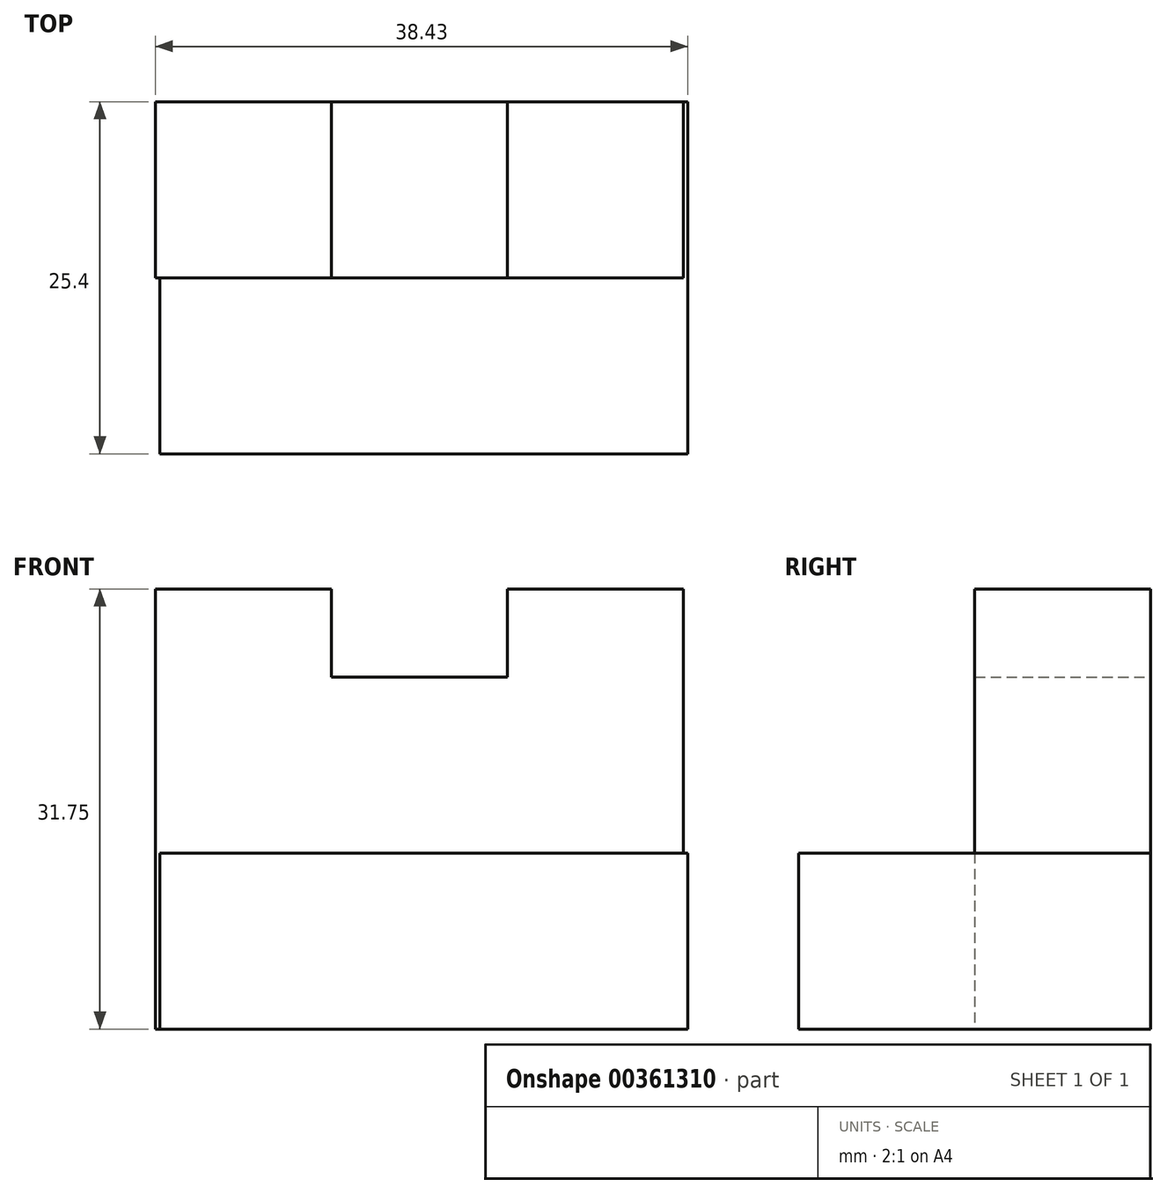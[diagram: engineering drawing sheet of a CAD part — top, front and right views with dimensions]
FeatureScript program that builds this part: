
annotation { "Feature Type Name" : "Feature", "Feature Type Description" : "" }
export const myFeature = defineFeature(function(context is Context, id is Id, definition is map)
    precondition{}
    {
        {
            var Q0;
            Q0=qCreatedBy(makeId("Front.planeOp"),FACE);
            var sketch = newSketch(context, id + "F0", { "sketchPlane" : qUnion([Q0])});
            skLineSegment(sketch, "E0", {"start": v(-25.4, 31.75) * mm, "end": v(-25.4, 0) * mm});
            skLineSegment(sketch, "E1", {"start": v(-25.4, 0) * mm, "end": v(12.7, 0) * mm});
            skLineSegment(sketch, "E2", {"start": v(12.7, 0) * mm, "end": v(12.7, 31.75) * mm});
            skLineSegment(sketch, "E3", {"start": v(-25.4, 31.75) * mm, "end": v(-12.7, 31.75) * mm});
            skLineSegment(sketch, "E4", {"start": v(12.7, 31.75) * mm, "end": v(0, 31.75) * mm});
            skLineSegment(sketch, "E5", {"start": v(-12.7, 31.75) * mm, "end": v(-12.7, 25.4) * mm});
            skLineSegment(sketch, "E6", {"start": v(0, 31.75) * mm, "end": v(0, 25.4) * mm});
            skLineSegment(sketch, "E7", {"start": v(-12.7, 25.4) * mm, "end": v(0, 25.4) * mm});
            skSolve(sketch);
        }
        {
            var Q0;
            Q0 = qSketchRegion(id + "F0", true);
            extrude(context, id + "F1", {"entities" : qUnion([Q0]), "depth" : 12.7 * mm});
        }
        {
            var Q0;
            Q0=qCreatedBy(makeId("Front.planeOp"),FACE);
            var sketch = newSketch(context, id + "F2", { "sketchPlane" : qUnion([Q0])});
            skLineSegment(sketch, "E8", {"start": v(-25.07, 0) * mm, "end": v(-25.07, 12.7) * mm});
            skLineSegment(sketch, "E9", {"start": v(-25.07, 12.7) * mm, "end": v(13.03, 12.7) * mm});
            skLineSegment(sketch, "E10", {"start": v(13.03, 12.7) * mm, "end": v(13.03, 0) * mm});
            skLineSegment(sketch, "E11", {"start": v(-25.07, 0) * mm, "end": v(13.03, 0) * mm});
            skSolve(sketch);
        }
        {
            var Q0;
            Q0 = qSketchRegion(id + "F2", true);
            extrude(context, id + "F3", {"entities" : qUnion([Q0]), "operationType" : NewBodyOperationType.ADD, "depth" : 25.4 * mm});
        }
    });
